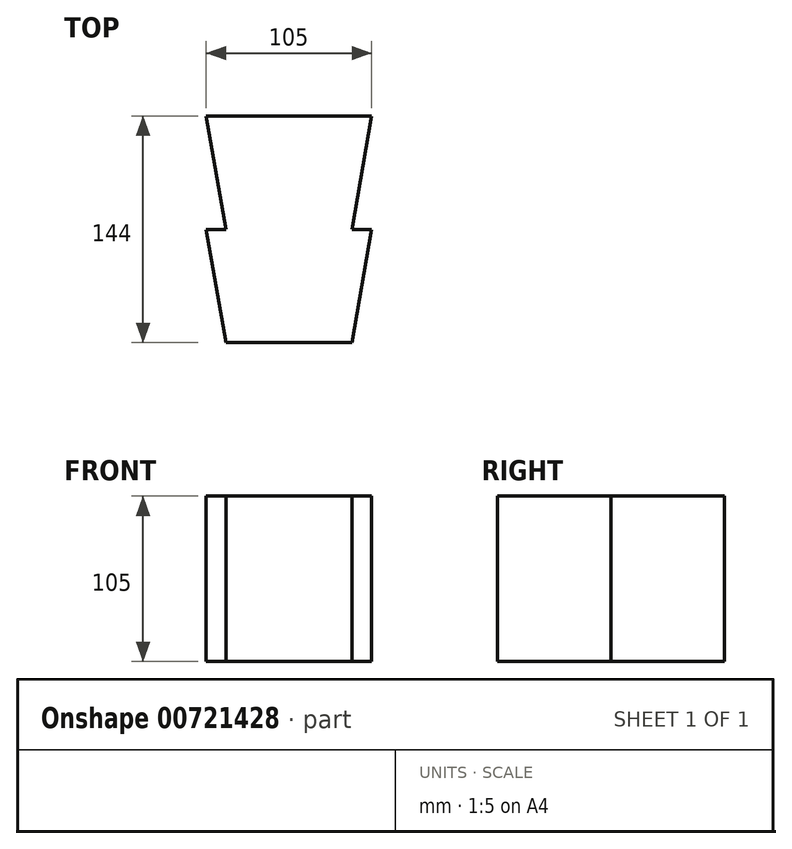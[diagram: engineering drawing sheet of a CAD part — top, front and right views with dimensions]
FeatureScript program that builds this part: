
annotation { "Feature Type Name" : "Feature", "Feature Type Description" : "" }
export const myFeature = defineFeature(function(context is Context, id is Id, definition is map)
    precondition{}
    {
        {
            var Q0;
            Q0=qCreatedBy(makeId("Top.planeOp"),FACE);
            var sketch = newSketch(context, id + "F0", { "sketchPlane" : qUnion([Q0])});
            skLineSegment(sketch, "E0", {"start": v(-40, 0) * mm, "end": v(40, 0) * mm});
            skLineSegment(sketch, "E1", {"start": v(-52.5, 72) * mm, "end": v(52.5, 72) * mm});
            skLineSegment(sketch, "E2", {"start": v(0, 72) * mm, "end": v(0, 0) * mm});
            skPoint(sketch, "E2.endSnap0", {"position": v(0, 0) * mm});
            skLineSegment(sketch, "E3", {"start": v(-52.5, 72) * mm, "end": v(-40, 0) * mm});
            skLineSegment(sketch, "E4", {"start": v(40, 0) * mm, "end": v(52.5, 72) * mm});
            skLineSegment(sketch, "E5", {"start": v(-40, -72) * mm, "end": v(40, -72) * mm});
            skPoint(sketch, "E6", {"position": v(0, -72) * mm});
            skLineSegment(sketch, "E7", {"start": v(0, -72) * mm, "end": v(0, 0) * mm});
            skLineSegment(sketch, "E8", {"start": v(-52.5, 0) * mm, "end": v(52.5, 0) * mm});
            skLineSegment(sketch, "E9", {"start": v(-52.5, 0) * mm, "end": v(-40, -72) * mm});
            skLineSegment(sketch, "E10", {"start": v(40, -72) * mm, "end": v(52.5, 0) * mm});
            skSolve(sketch);
        }
        {
            var Q0;
            Q0 = qSketchRegion(id + "F0", true);
            extrude(context, id + "F1", {"entities" : qUnion([Q0]), "depth" : 105 * mm, "offsetDistance" : 25 * mm});
        }
    });
